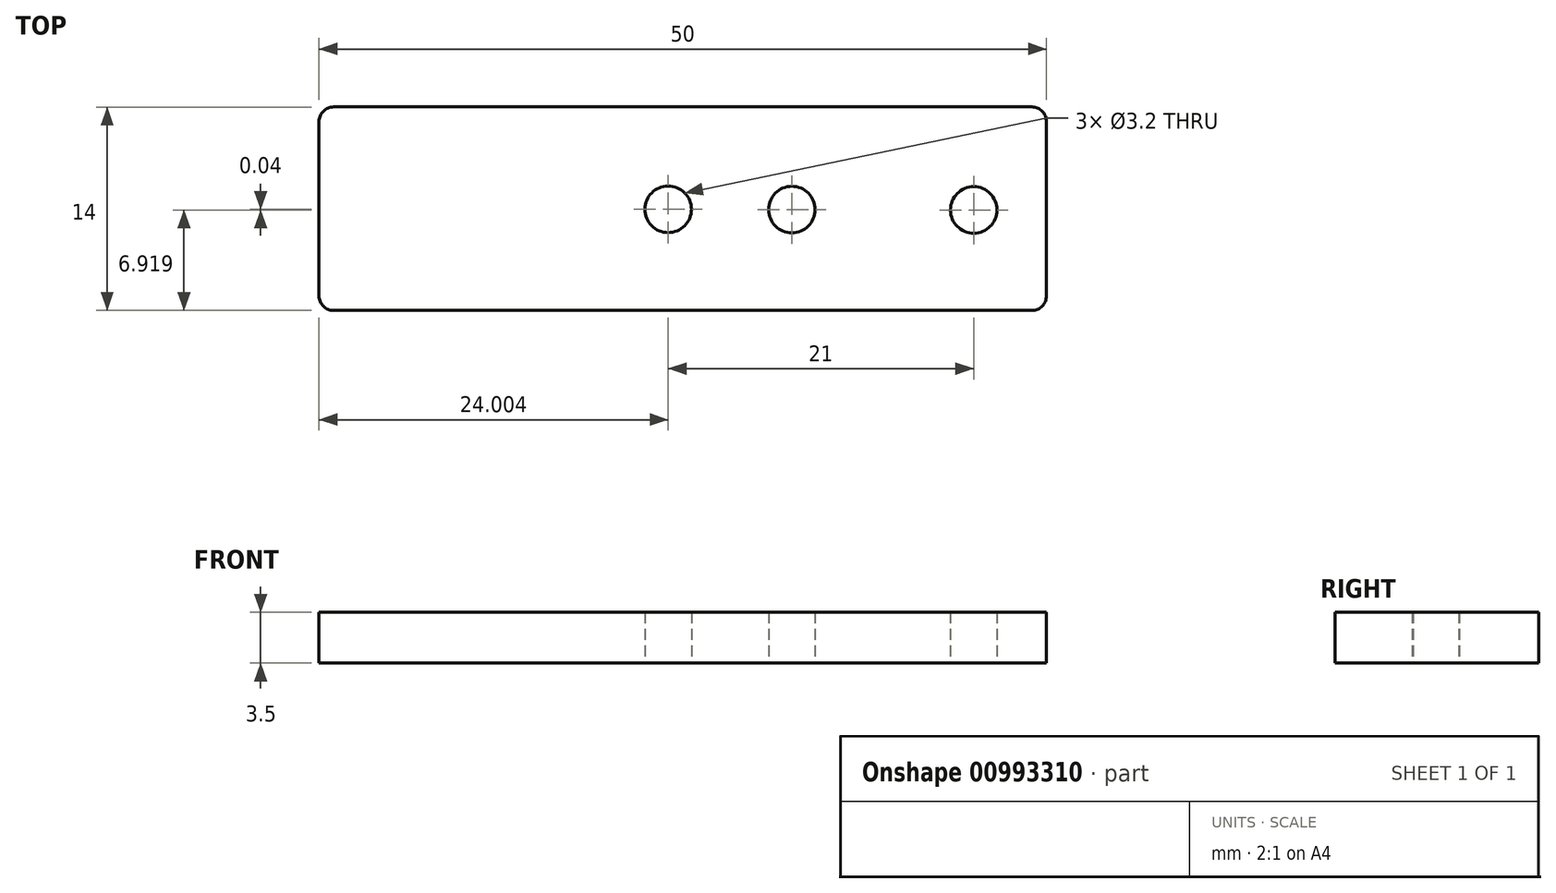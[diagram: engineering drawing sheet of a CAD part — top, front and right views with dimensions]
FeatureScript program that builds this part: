
annotation { "Feature Type Name" : "Feature", "Feature Type Description" : "" }
export const myFeature = defineFeature(function(context is Context, id is Id, definition is map)
    precondition{}
    {
        {
            var Q0;
            Q0=qCreatedBy(makeId("Top.planeOp"),FACE);
            var sketch = newSketch(context, id + "F0", { "sketchPlane" : qUnion([Q0])});
            skLineSegment(sketch, "E0.bottom", {"start": v(-24.24, 7.1) * mm, "end": v(23.76, 7.1) * mm});
            skLineSegment(sketch, "E0.top", {"start": v(-24.24, -6.9) * mm, "end": v(23.76, -6.9) * mm});
            skLineSegment(sketch, "E0.left", {"start": v(-25.24, 6.1) * mm, "end": v(-25.24, -5.9) * mm});
            skLineSegment(sketch, "E0.right", {"start": v(24.76, 6.1) * mm, "end": v(24.76, -5.9) * mm});
            skPoint(sketch, "E1.visualSharp", {"position": v(-25.24, 7.1) * mm});
            skArc(sketch, "E1.filletArc", {"start": v(-24.24, 7.1) * mm, "mid": v(-24.94, 6.8) * mm, "end": v(-25.24, 6.1) * mm});
            skPoint(sketch, "E2.visualSharp", {"position": v(-25.24, -6.9) * mm});
            skArc(sketch, "E2.filletArc", {"start": v(-25.24, -5.9) * mm, "mid": v(-24.94, -6.61) * mm, "end": v(-24.24, -6.9) * mm});
            skPoint(sketch, "E3.visualSharp", {"position": v(24.76, 7.1) * mm});
            skArc(sketch, "E3.filletArc", {"start": v(24.76, 6.1) * mm, "mid": v(24.47, 6.8) * mm, "end": v(23.76, 7.1) * mm});
            skPoint(sketch, "E4.visualSharp", {"position": v(24.76, -6.9) * mm});
            skArc(sketch, "E4.filletArc", {"start": v(23.76, -6.9) * mm, "mid": v(24.47, -6.61) * mm, "end": v(24.76, -5.9) * mm});
            skLineSegment(sketch, "E5", {"start": v(-25.24, 0.1) * mm, "end": v(24.76, 0) * mm, "construction": true});
            skCircle(sketch, "E6", {"center": v(-1.24, 0.05) * mm, "radius": 1.6 * mm});
            skCircle(sketch, "E7", {"center": v(7.26, 0.03) * mm, "radius": 1.6 * mm});
            skCircle(sketch, "E8", {"center": v(19.76, 0) * mm, "radius": 1.6 * mm});
            skSolve(sketch);
        }
        {
            var Q0;
            Q0=makeQuery(id+"F0.imprint","IMPRINT",FACE,{"disambiguationData":[TD([[makeQuery(id+"F0.imprint","IMPRINT",EDGE,{"derivedFrom":sQuery(id+"F0.wireOp",EDGE,"E0.bottom")}),-1.0]])]});
            extrude(context, id + "F1", {"entities" : qUnion([Q0]), "depth" : 3.5 * mm, "offsetDistance" : 25 * mm});
        }
    });
